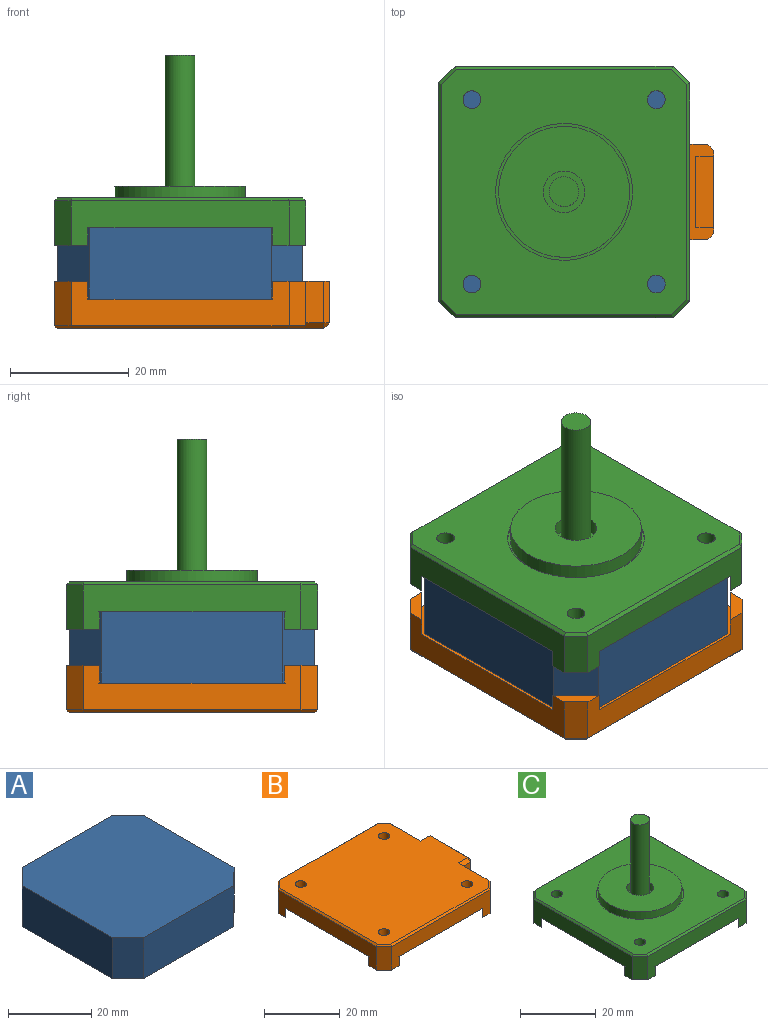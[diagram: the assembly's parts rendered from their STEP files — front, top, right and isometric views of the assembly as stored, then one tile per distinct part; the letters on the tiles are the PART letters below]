
ASSEMBLY  parts=3 mates=2
PART A: 10 faces, bbox 41.3x41.3x12 mm
  f0: plane 30.57x12mm, normal (0,1,0), area 366.9mm2, adj f1,f7,f8,f9
  f1: plane 12x5.36mm, normal (-0.71,0.71,0), area 91mm2, adj f0,f2,f8,f9
  f2: plane 30.57x12mm, normal (-1,0,0), area 366.9mm2, adj f1,f3,f8,f9
  f3: plane 12x5.36mm, normal (-0.71,-0.71,0), area 91mm2, adj f2,f4,f8,f9
  f4: plane 30.57x12mm, normal (0,-1,0), area 366.9mm2, adj f3,f5,f8,f9
  f5: plane 12x5.36mm, normal (0.71,-0.71,0), area 91mm2, adj f4,f6,f8,f9
  f6: plane 30.57x12mm, normal (1,0,0), area 366.9mm2, adj f5,f7,f8,f9
  f7: plane 12x5.36mm, normal (0.71,0.71,0), area 91mm2, adj f0,f6,f8,f9
  f8: plane 41.3x41.3mm, normal (0,0,1), area 1648.1mm2, adj f0,f1,f2,f3,f4,f5,f6,f7
  f9: plane 41.3x41.3mm, normal (0,0,-1), area 1648.1mm2, adj f0,f1,f2,f3,f4,f5,f6,f7
PART B: 48 faces, bbox 46.3x42.3x8 mm
  f0: plane 42.3x42.3mm, normal (0,0,-1), area 1697mm2, adj f1,f3,f5,f7,f9,f12,f13,f14
  f1: plane 10.82x7.5mm, normal (1,0,0), area 55.1mm2, adj f0,f2,f15,f22,f23,f32,f39
  f2: plane 7.5x2.83mm, normal (0.71,0.71,0), area 30mm2, adj f1,f3,f23,f40
  f3: plane 36.64x7.5mm, normal (0,1,0), area 181.9mm2, adj f0,f2,f4,f20,f21,f22,f23,f41
  f4: plane 7.5x2.83mm, normal (-0.71,0.71,0), area 30mm2, adj f3,f5,f21,f42
  f5: plane 36.64x7.5mm, normal (-1,0,0), area 181.9mm2, adj f0,f4,f6,f18,f19,f20,f21,f43
  f6: plane 7.5x2.83mm, normal (-0.71,-0.71,0), area 30mm2, adj f5,f7,f19,f44
  f7: plane 36.64x7.5mm, normal (0,-1,0), area 181.9mm2, adj f0,f6,f8,f18,f19,f29,f30,f45
  f8: plane 7.5x2.83mm, normal (0.71,-0.71,0), area 30mm2, adj f7,f9,f30,f46
  f9: plane 10.82x7.5mm, normal (1,0,0), area 55.1mm2, adj f0,f8,f10,f29,f30,f35,f47
  f10: plane 7x3mm, normal (0,-1,0), area 21mm2, adj f9,f25,f28,f35,f38
  f11: plane 14x7mm, normal (1,0,0), area 38mm2, adj f24,f26,f28,f31,f33,f36,f38
  f12: cylinder r=1.5mm len=5mm, axis (0,0,-1), area 47.1mm2, adj f0,f17
  f13: cylinder r=1.5mm len=5mm, axis (0,0,-1), area 47.1mm2, adj f0,f17
  f14: cylinder r=1.5mm len=5mm, axis (0,0,-1), area 47.1mm2, adj f0,f17
  f15: plane 7x3mm, normal (0,1,0), area 21mm2, adj f1,f25,f28,f32,f33
  f16: cylinder r=1.5mm len=5mm, axis (0,0,-1), area 47.1mm2, adj f0,f17
  f17: plane 44.8x41.3mm, normal (0,0,1), area 1713.6mm2, adj f12,f13,f14,f16,f32,f35,f36,f39
  f18: plane 5.66x5.66mm, normal (0.71,0.71,0), area 24mm2, adj f0,f5,f7,f19
  f19: plane 5.66x5.66mm, normal (0,0,-1), area 12mm2, adj f5,f6,f7,f18
  f20: plane 5.66x5.66mm, normal (0.71,-0.71,0), area 24mm2, adj f0,f3,f5,f21
  f21: plane 5.66x5.66mm, normal (0,0,-1), area 12mm2, adj f3,f4,f5,f20
  f22: plane 5.66x5.66mm, normal (-0.71,-0.71,0), area 24mm2, adj f0,f1,f3,f23
  f23: plane 5.66x5.66mm, normal (0,0,-1), area 12mm2, adj f1,f2,f3,f22
  f24: plane 5x3mm, normal (0,-1,0), area 15mm2, adj f11,f27,f28,f31
  f25: plane 16x3mm, normal (-1,0,0), area 48mm2, adj f0,f10,f15,f28
  f26: plane 5x3mm, normal (0,1,0), area 15mm2, adj f11,f27,f28,f31
  f27: plane 12x5mm, normal (1,0,0), area 60mm2, adj f24,f26,f28,f31
  f28: plane 16x4mm, normal (0,0,-1), area 27mm2, adj f10,f11,f15,f24,f25,f26,f27,f33
  f29: plane 5.66x5.66mm, normal (-0.71,0.71,0), area 24mm2, adj f0,f7,f9,f30
  f30: plane 5.66x5.66mm, normal (0,0,-1), area 12mm2, adj f7,f8,f9,f29
  f31: plane 12x3mm, normal (0,0,-1), area 36mm2, adj f11,f24,f26,f27
  f32: plane 3.5x1mm, normal (0,0.71,0.71), area 4.4mm2, adj f1,f15,f17,f34,f39
  f33: plane 7x1mm, normal (0.71,0.71,0), area 9.9mm2, adj f11,f15,f28,f34
  f34: plane 1x1mm, normal (0.58,0.58,0.58), area 0.9mm2, adj f32,f33,f36
  f35: plane 3.5x1mm, normal (0,-0.71,0.71), area 4.4mm2, adj f9,f10,f17,f37,f47
  f36: plane 14x1mm, normal (0.71,0,0.71), area 19.8mm2, adj f11,f17,f34,f37
  f37: plane 1x1mm, normal (0.58,-0.58,0.58), area 0.9mm2, adj f35,f36,f38
  f38: plane 7x1mm, normal (0.71,-0.71,0), area 9.9mm2, adj f10,f11,f28,f37
  f39: plane 11.32x0.5mm, normal (0.71,0,0.71), area 7.8mm2, adj f1,f17,f32,f40
  f40: plane 3.04x3.04mm, normal (0.5,0.5,0.71), area 2.7mm2, adj f2,f17,f39,f41
  f41: plane 36.64x0.5mm, normal (0,0.71,0.71), area 25.8mm2, adj f3,f17,f40,f42
  f42: plane 3.04x3.04mm, normal (-0.5,0.5,0.71), area 2.7mm2, adj f4,f17,f41,f43
  f43: plane 36.64x0.5mm, normal (-0.71,0,0.71), area 25.8mm2, adj f5,f17,f42,f44
  f44: plane 3.04x3.04mm, normal (-0.5,-0.5,0.71), area 2.7mm2, adj f6,f17,f43,f45
  f45: plane 36.64x0.5mm, normal (0,-0.71,0.71), area 25.8mm2, adj f7,f17,f44,f46
  f46: plane 3.04x3.04mm, normal (0.5,-0.5,0.71), area 2.7mm2, adj f8,f17,f45,f47
  f47: plane 11.32x0.5mm, normal (0.71,0,0.71), area 7.8mm2, adj f9,f17,f35,f46
PART C: 38 faces, bbox 42.3x42.3x32 mm
  f0: plane 36.64x7.5mm, normal (-1,0,0), area 181.9mm2, adj f1,f10,f13,f14,f15,f20,f21,f32
  f1: plane 7.5x2.83mm, normal (-0.71,-0.71,0), area 30mm2, adj f0,f2,f15,f34
  f2: plane 36.64x7.5mm, normal (0,-1,0), area 181.9mm2, adj f1,f3,f13,f14,f15,f16,f17,f36
  f3: plane 7.5x2.83mm, normal (0.71,-0.71,0), area 30mm2, adj f2,f4,f17,f37
  f4: plane 36.64x7.5mm, normal (1,0,0), area 181.9mm2, adj f3,f5,f13,f16,f17,f18,f19,f35
  f5: plane 7.5x2.83mm, normal (0.71,0.71,0), area 30mm2, adj f4,f6,f19,f33
  f6: plane 36.64x7.5mm, normal (0,1,0), area 181.9mm2, adj f5,f10,f13,f18,f19,f20,f21,f31
  f7: cylinder r=1.5mm len=5mm, axis (0,0,-1), area 47.1mm2, adj f12,f13
  f8: cylinder r=1.5mm len=5mm, axis (0,0,-1), area 47.1mm2, adj f12,f13
  f9: cylinder r=1.5mm len=5mm, axis (0,0,-1), area 47.1mm2, adj f12,f13
  f10: plane 7.5x2.83mm, normal (-0.71,0.71,0), area 30mm2, adj f0,f6,f21,f30
  f11: cylinder r=1.5mm len=5mm, axis (0,0,-1), area 47.1mm2, adj f12,f13
  f12: plane 41.3x41.3mm, normal (0,0,1), area 1249.1mm2, adj f7,f8,f9,f11,f23,f30,f31,f32
  f13: plane 42.3x42.3mm, normal (0,0,-1), area 1697mm2, adj f0,f2,f4,f6,f7,f8,f9,f11
  f14: plane 5.66x5.66mm, normal (0.71,0.71,0), area 24mm2, adj f0,f2,f13,f15
  f15: plane 5.66x5.66mm, normal (0,0,-1), area 12mm2, adj f0,f1,f2,f14
  f16: plane 5.66x5.66mm, normal (-0.71,0.71,0), area 24mm2, adj f2,f4,f13,f17
  f17: plane 5.66x5.66mm, normal (0,0,-1), area 12mm2, adj f2,f3,f4,f16
  f18: plane 5.66x5.66mm, normal (-0.71,-0.71,0), area 24mm2, adj f4,f6,f13,f19
  f19: plane 5.66x5.66mm, normal (0,0,-1), area 12mm2, adj f4,f5,f6,f18
  f20: plane 5.66x5.66mm, normal (0.71,-0.71,0), area 24mm2, adj f0,f6,f13,f21
  f21: plane 5.66x5.66mm, normal (0,0,-1), area 12mm2, adj f0,f6,f10,f20
  f22: cylinder r=11mm len=22mm, axis (0,0,-1), area 172.8mm2, adj f24,f25
  f23: cylinder r=11.5mm len=23mm, axis (0,0,-1), area 36.1mm2, adj f12,f24
  f24: plane 23x23mm, normal (0,0,1), area 35.3mm2, adj f22,f23
  f25: plane 22x22mm, normal (0,0,1), area 341.6mm2, adj f22,f27
  f26: cylinder r=2.5mm len=24.5mm, axis (0,0,-1), area 384.8mm2, adj f28,f29
  f27: cylinder r=3.5mm len=7mm, axis (0,0,-1), area 55mm2, adj f25,f28
  f28: plane 7x7mm, normal (0,0,1), area 18.8mm2, adj f26,f27
  f29: plane 5x5mm, normal (0,0,1), area 19.6mm2, adj f26
  f30: plane 3.04x3.04mm, normal (-0.5,0.5,0.71), area 2.7mm2, adj f10,f12,f31,f32
  f31: plane 36.64x0.5mm, normal (0,0.71,0.71), area 25.8mm2, adj f6,f12,f30,f33
  f32: plane 36.64x0.5mm, normal (-0.71,0,0.71), area 25.8mm2, adj f0,f12,f30,f34
  f33: plane 3.04x3.04mm, normal (0.5,0.5,0.71), area 2.7mm2, adj f5,f12,f31,f35
  f34: plane 3.04x3.04mm, normal (-0.5,-0.5,0.71), area 2.7mm2, adj f1,f12,f32,f36
  f35: plane 36.64x0.5mm, normal (0.71,0,0.71), area 25.8mm2, adj f4,f12,f33,f37
  f36: plane 36.64x0.5mm, normal (0,-0.71,0.71), area 25.8mm2, adj f2,f12,f34,f37
  f37: plane 3.04x3.04mm, normal (0.5,-0.5,0.71), area 2.7mm2, adj f3,f12,f35,f36
PLACE A t=(-62.3,0,-12)mm
PLACE B rot(axis=(1,0,0),180deg) t=(0,104.6,-12)mm
PLACE C at identity fixed
MATE fastened B.f0 <-> A.f9  axis (0,0,1) through (0,0,-12)mm
MATE fastened C.f23 <-> A.f8  axis (0,0,-1) through (0,0,0)mm
